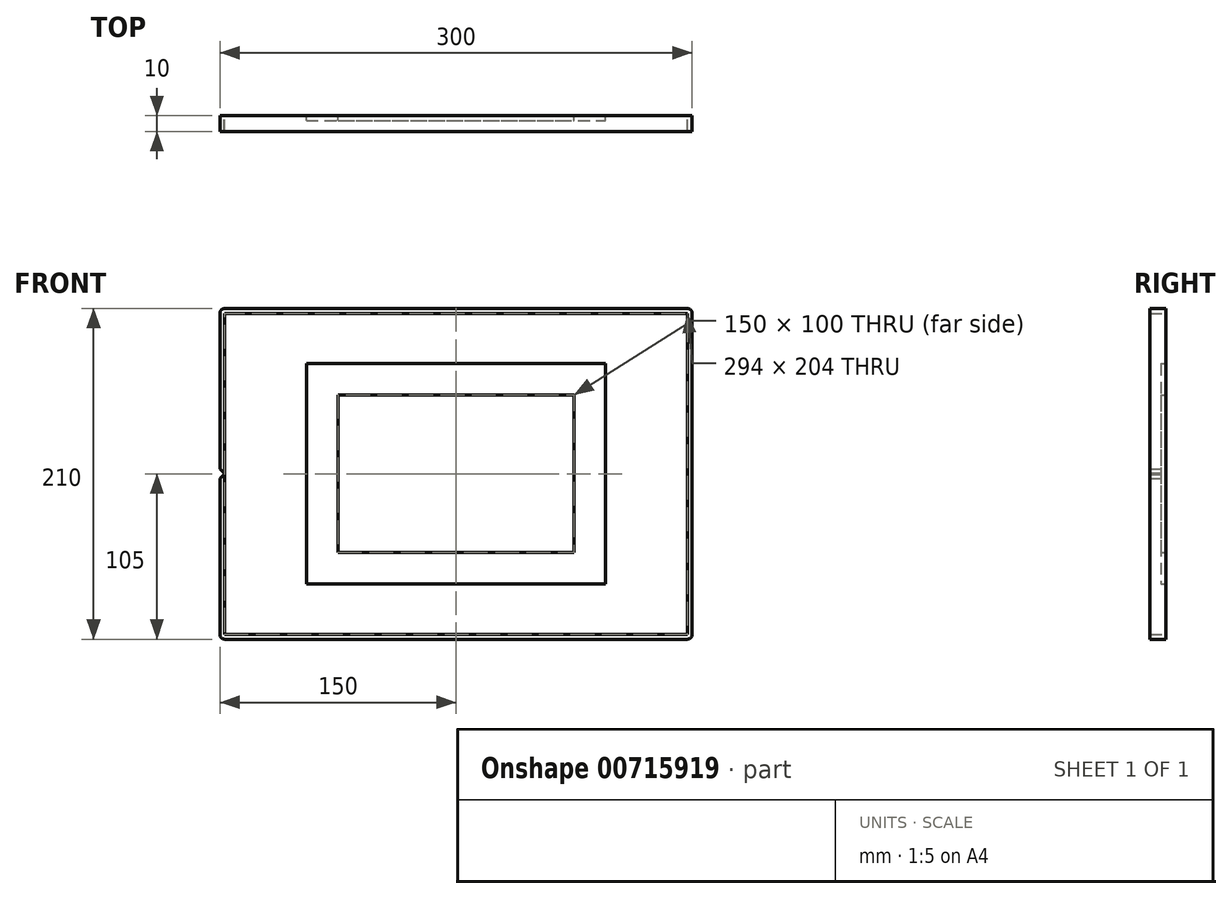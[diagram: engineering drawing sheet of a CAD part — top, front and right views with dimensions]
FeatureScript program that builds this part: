
annotation { "Feature Type Name" : "Feature", "Feature Type Description" : "" }
export const myFeature = defineFeature(function(context is Context, id is Id, definition is map)
    precondition{}
    {
        {
            var Q0;
            Q0=qCreatedBy(makeId("Front.planeOp"),FACE);
            var sketch = newSketch(context, id + "F0", { "sketchPlane" : qUnion([Q0])});
            skLineSegment(sketch, "E0.bottom", {"start": v(-147, 105) * mm, "end": v(147, 105) * mm});
            skLineSegment(sketch, "E0.top", {"start": v(-147, -105) * mm, "end": v(147, -105) * mm});
            skLineSegment(sketch, "E0.left", {"start": v(-150, 102) * mm, "end": v(-150, 3) * mm});
            skLineSegment(sketch, "E0.right", {"start": v(150, 102) * mm, "end": v(150, -102) * mm});
            skPoint(sketch, "E0.middle", {"position": v(0, 0) * mm});
            skPoint(sketch, "E1.visualSharp", {"position": v(-150, 105) * mm});
            skArc(sketch, "E1.filletArc", {"start": v(-147, 105) * mm, "mid": v(-149.12, 104.12) * mm, "end": v(-150, 102) * mm});
            skPoint(sketch, "E2.visualSharp", {"position": v(-150, -105) * mm});
            skArc(sketch, "E2.filletArc", {"start": v(-150, -102) * mm, "mid": v(-149.12, -104.12) * mm, "end": v(-147, -105) * mm});
            skPoint(sketch, "E3.visualSharp", {"position": v(150, 105) * mm});
            skArc(sketch, "E3.filletArc", {"start": v(150, 102) * mm, "mid": v(149.12, 104.12) * mm, "end": v(147, 105) * mm});
            skPoint(sketch, "E4.visualSharp", {"position": v(150, -105) * mm});
            skArc(sketch, "E4.filletArc", {"start": v(147, -105) * mm, "mid": v(149.12, -104.12) * mm, "end": v(150, -102) * mm});
            skLineSegment(sketch, "E5", {"start": v(-150, 0) * mm, "end": v(150, 0) * mm, "construction": true});
            skLineSegment(sketch, "E6.bottom", {"start": v(-147, 102) * mm, "end": v(147, 102) * mm});
            skLineSegment(sketch, "E6.top", {"start": v(-147, -102) * mm, "end": v(147, -102) * mm});
            skLineSegment(sketch, "E6.left", {"start": v(-147, 102) * mm, "end": v(-147, -102) * mm});
            skLineSegment(sketch, "E6.right", {"start": v(147, 102) * mm, "end": v(147, -102) * mm});
            skLineSegment(sketch, "E7", {"start": v(-147.42, 0.42) * mm, "end": v(-150, 3) * mm});
            skLineSegment(sketch, "E8", {"start": v(-147.42, -0.42) * mm, "end": v(-150, -3) * mm});
            skLineSegment(sketch, "E9.trimOffspring", {"start": v(-150, -3) * mm, "end": v(-150, -102) * mm});
            skLineSegment(sketch, "E10", {"start": v(-147.42, 0.42) * mm, "end": v(-147.42, -0.42) * mm});
            skPoint(sketch, "E11.orphan", {"position": v(-147, 0) * mm});
            skLineSegment(sketch, "E12.bottom", {"start": v(-95, 70) * mm, "end": v(95, 70) * mm});
            skLineSegment(sketch, "E12.top", {"start": v(-95, -70) * mm, "end": v(95, -70) * mm});
            skLineSegment(sketch, "E12.left", {"start": v(-95, 70) * mm, "end": v(-95, -70) * mm});
            skLineSegment(sketch, "E12.right", {"start": v(95, 70) * mm, "end": v(95, -70) * mm});
            skLineSegment(sketch, "E13.bottom", {"start": v(-75, 50) * mm, "end": v(75, 50) * mm});
            skLineSegment(sketch, "E13.top", {"start": v(-75, -50) * mm, "end": v(75, -50) * mm});
            skLineSegment(sketch, "E13.left", {"start": v(-75, 50) * mm, "end": v(-75, -50) * mm});
            skLineSegment(sketch, "E13.right", {"start": v(75, 50) * mm, "end": v(75, -50) * mm});
            skLineSegment(sketch, "E14", {"start": v(-95, 70) * mm, "end": v(-75, 50) * mm});
            skLineSegment(sketch, "E15", {"start": v(-75, -50) * mm, "end": v(-95, -70) * mm});
            skLineSegment(sketch, "E16", {"start": v(75, -50) * mm, "end": v(95, -70) * mm});
            skLineSegment(sketch, "E17", {"start": v(75, 50) * mm, "end": v(95, 70) * mm});
            skSolve(sketch);
        }
        {
            var Q0;
            Q0 = qSketchRegion(id + "F0", true);
            extrude(context, id + "F1", {"entities" : qUnion([Q0]), "depth" : 10 * mm, "offsetDistance" : 25 * mm});
        }
        {
            var Q0;
            Q0=makeQuery(id+"F0.imprint","IMPRINT",FACE,{"disambiguationData":[TD([[makeQuery(id+"F0.imprint","IMPRINT",EDGE,{"derivedFrom":sQuery(id+"F0.wireOp",EDGE,"E12.left")}),1.0]])]});
            var Q1;
            Q1=makeQuery(id+"F0.imprint","IMPRINT",FACE,{"disambiguationData":[TD([[makeQuery(id+"F0.imprint","IMPRINT",EDGE,{"derivedFrom":sQuery(id+"F0.wireOp",EDGE,"E12.bottom")}),-1.0]])]});
            var Q2;
            Q2=makeQuery(id+"F0.imprint","IMPRINT",FACE,{"disambiguationData":[TD([[makeQuery(id+"F0.imprint","IMPRINT",EDGE,{"derivedFrom":sQuery(id+"F0.wireOp",EDGE,"E12.right")}),-1.0]])]});
            var Q3;
            Q3=makeQuery(id+"F0.imprint","IMPRINT",FACE,{"disambiguationData":[TD([[makeQuery(id+"F0.imprint","IMPRINT",EDGE,{"derivedFrom":sQuery(id+"F0.wireOp",EDGE,"E12.top")}),1.0]])]});
            extrude(context, id + "F2", {"entities" : qUnion([Q0, Q1, Q2, Q3]), "depth" : 3 * mm, "offsetDistance" : 25 * mm});
        }
    });
